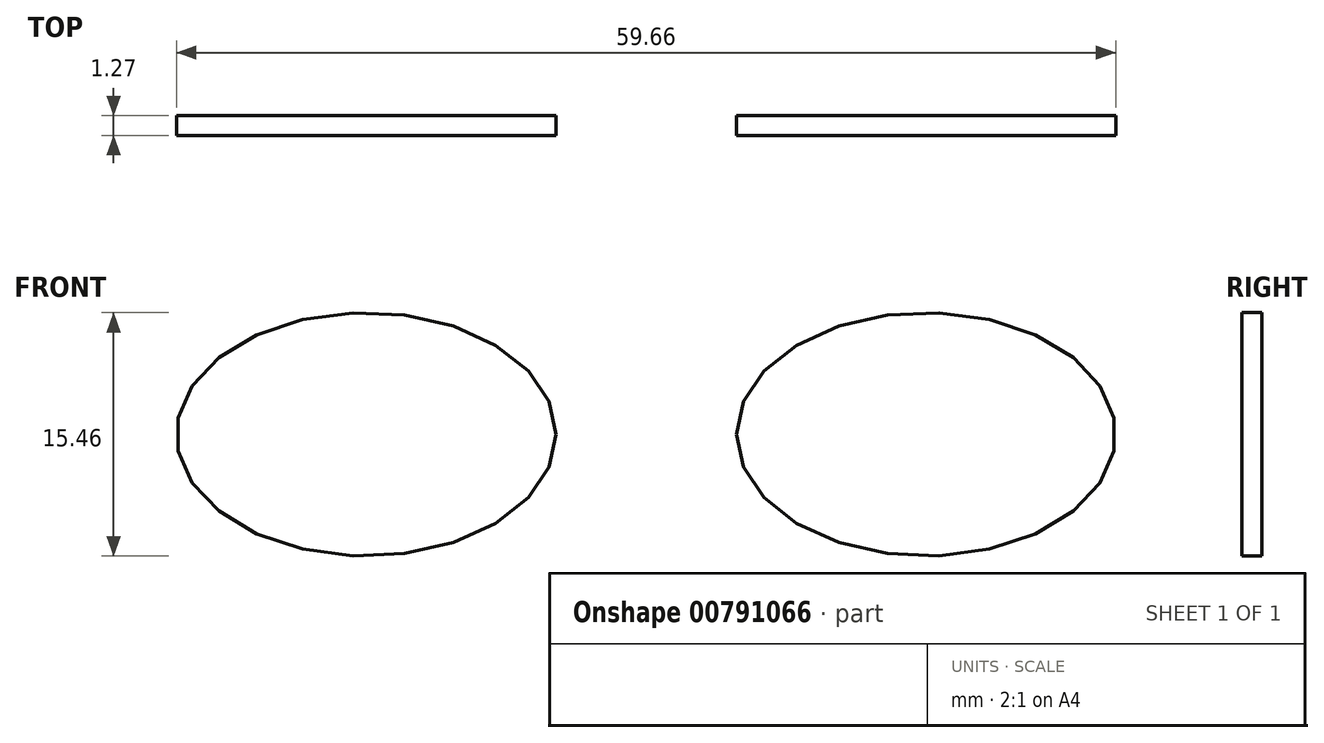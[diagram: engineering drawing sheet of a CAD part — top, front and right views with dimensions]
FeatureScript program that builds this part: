
annotation { "Feature Type Name" : "Feature", "Feature Type Description" : "" }
export const myFeature = defineFeature(function(context is Context, id is Id, definition is map)
    precondition{}
    {
        {
            var Q0;
            Q0=qCreatedBy(makeId("Front.planeOp"),FACE);
            var sketch = newSketch(context, id + "F0", { "sketchPlane" : qUnion([Q0])});
            skEllipse(sketch, "E0", {"center": v(-17.78, 0) * mm, "majorRadius": 12.05 * mm, "minorRadius": 7.73 * mm, "majorAxis": v(1, 0)});
            skEllipse(sketch, "E1.MirrorC", {"center": v(17.78, 0) * mm, "majorRadius": 12.05 * mm, "minorRadius": 7.73 * mm, "majorAxis": v(-1, 0)});
            skSolve(sketch);
        }
        {
            var Q0;
            Q0=sQuery(id+"F0.wireOp",EDGE,"E0");
            extrude(context, id + "F1", {"bodyType" : ToolBodyType.SURFACE, "surfaceEntities" : qUnion([Q0]), "oppositeDirection" : true, "depth" : 1.27 * mm, "offsetDistance" : 25.4 * mm});
        }
        {
            var Q0;
            Q0=makeQuery(id+"F0.imprint","IMPRINT",FACE,{"disambiguationData":[TD([[makeQuery(id+"F0.imprint","IMPRINT",EDGE,{"derivedFrom":sQuery(id+"F0.wireOp",EDGE,"E1.MirrorC")}),1.0]])]});
            var Q1;
            Q1=sQuery(id+"F0.wireOp",EDGE,"E1.MirrorC");
            extrude(context, id + "F2", {"entities" : qUnion([Q0]), "bodyType" : ToolBodyType.SURFACE, "surfaceEntities" : qUnion([Q1]), "oppositeDirection" : true, "depth" : 1.27 * mm, "offsetDistance" : 25.4 * mm});
        }
    });
